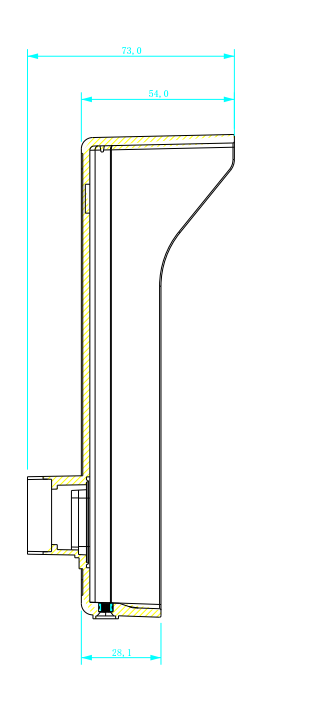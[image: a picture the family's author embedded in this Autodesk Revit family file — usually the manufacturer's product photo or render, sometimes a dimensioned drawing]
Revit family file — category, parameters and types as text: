
# Revit family: SP-03F
name_source: partatom
category: Устройства связи
units: mm (PartAtom-declared; Revit-internal decimal feet)

## family parameters
Всегда вертикально = Нет
На основе рабочей плоскости = Да
Общий = Да
При загрузке вырезать с полостями = Нет
Размер круглого соединителя = Использовать диаметр
Сохранять ориентацию аннотаций = Нет
Тип детали = Нормальный
Точка расчета площади = Нет

## types (1)
- SP-03F
    ADSK_URL документации изделия = https://drive.google.com
    ADSK_URL страницы изделия = https://www.bas-ip.com.ua
    ADSK_Версия Revit = Revit 2020
    ADSK_Единица измерения = шт
    ADSK_Завод-изготовитель = BAS-IP
    ADSK_Классификация нагрузок = Абонентское аудиоустройство
    ADSK_Количество фаз = 1
    ADSK_Коэффициент мощности = 0.9
    ADSK_Марка = SP-03F
    ADSK_Наименование = Абонентское аудиоустройство SP-03F
    ADSK_Наименование краткое = SP-03F
    ADSK_Напряжение = 12 В
    ADSK_Номинальная мощность = 0 Вт
    ADSK_Полная мощность = 0 В·А
    ADSK_Размер_Длина = 184 мм
    ADSK_Размер_Толщина = 28 мм
    ADSK_Размер_Ширина = 106 мм
    BIM library = https://bimlib.ru
    URL = https://www.bas-ip.ru
    Бесшумный режим = Да
    Вес упаковки = 0.58 кг
    Вызов лифта на этаж = Да
    Группа модели = Абонентское аудиоустройство
    Дополнительная функция = Кнопка звонка
    Звонки консьержу = Да
    Изготовитель = BAS-IP
    Изображение типоразмера = <Нет>
    Источник питания = PoE, +12 V DC (+11% -6%)
    Количество клавиш управления = 6
    Количество поддерживаемых учетных записей VoIP = 1
    Корпус = Пластик
    Метод конфигурации и программирования = WEB-интерфейс
    Модуль Wi-Fi = Да, для подключения к локальной сети
    Описание = Абонентское аудиоустройство SP-03F - Абонентское IP аудио устройство с поддержкой SIP, P2P и внутреннего протокола BAS-IP
    Открытие замка = Да
    Отметка по умолчанию = 0 мм
    Отображение различных состояний устройства с помощью светодиодов = Да
    Переадресация звонков = Да
    Поддерживаемый тип кодека = G.711μ/A
    Поддержка внутреннего протокола BAS-IP = Да
    Поддержка протокола SIP 2.0, для организации связи с любым VoIP оборудованием, поддерживающим этот протокол = Да
    Подключение к сети = 1 PoE порт IEEE 802.3af
    Размеры = 106×184×28 мм
    Размеры упаковки = 235×138.5×63 мм
    Режим "Не беспокоить" = Да
    Способ установки = Настенный монтаж
    Тип поддерживаемого протокола = IPv4
    Цветовое решение = Черный, белый
